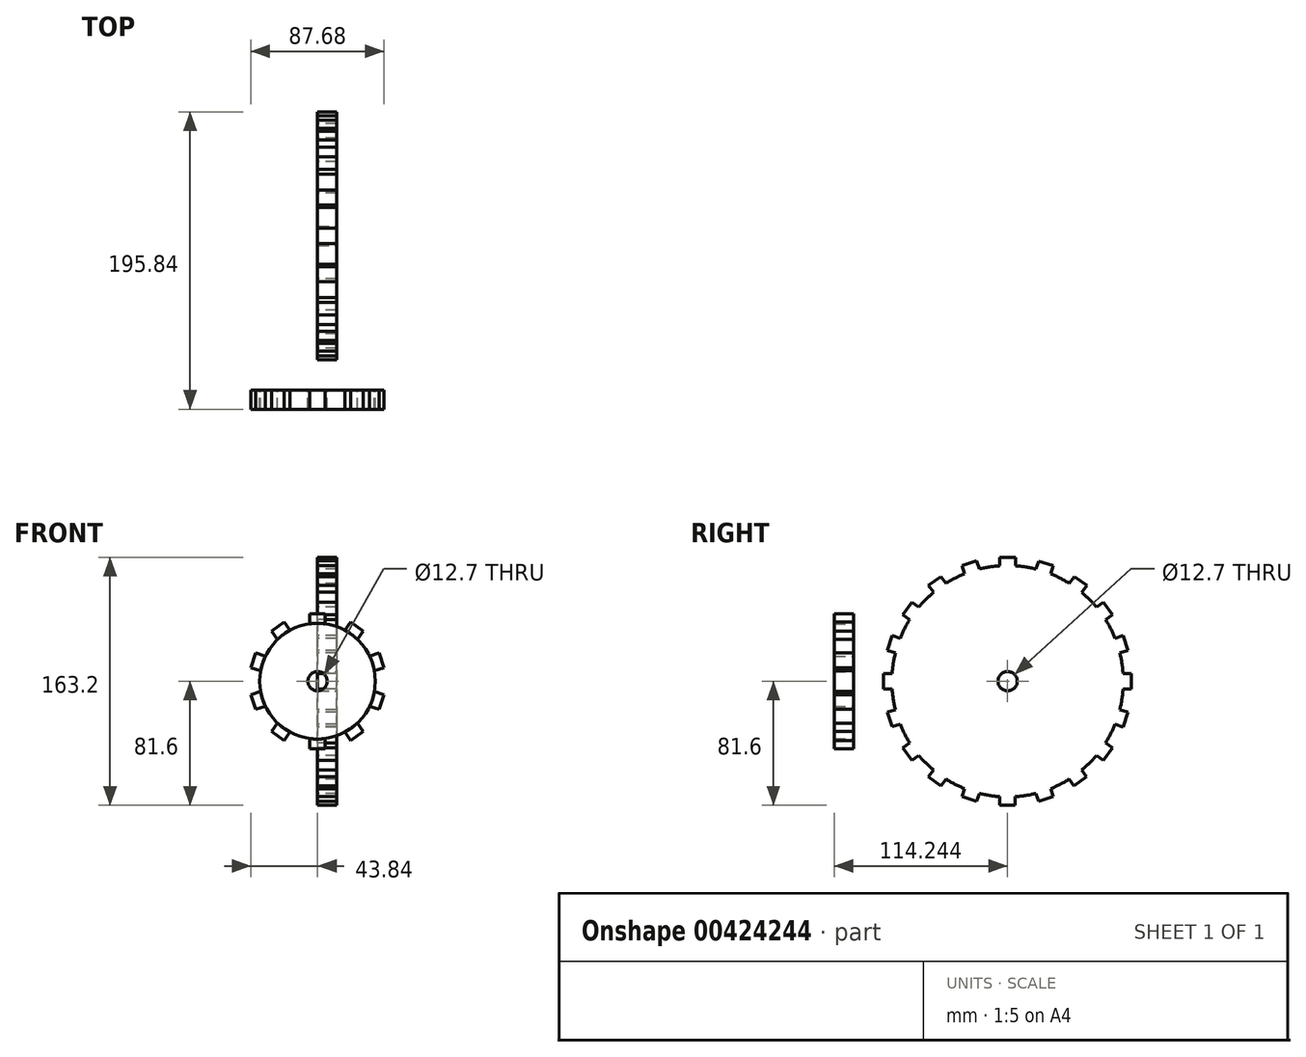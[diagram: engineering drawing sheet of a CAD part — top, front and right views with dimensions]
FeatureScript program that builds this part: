
annotation { "Feature Type Name" : "Feature", "Feature Type Description" : "" }
export const myFeature = defineFeature(function(context is Context, id is Id, definition is map)
    precondition{}
    {
        {
            var Q0;
            Q0=qCreatedBy(makeId("Front.planeOp"),FACE);
            var sketch = newSketch(context, id + "F0", { "sketchPlane" : qUnion([Q0])});
            skCircle(sketch, "E0", {"center": v(0, 0) * mm, "radius": 38.1 * mm});
            skSolve(sketch);
        }
        {
            var Q0;
            Q0=makeQuery(id+"F0.imprint","IMPRINT",FACE,{"disambiguationData":[TD([[makeQuery(id+"F0.imprint","IMPRINT",EDGE,{"derivedFrom":sQuery(id+"F0.wireOp",EDGE,"E0")}),1.0]])]});
            var sketch = newSketch(context, id + "F1", { "sketchPlane" : qUnion([Q0])});
            skLineSegment(sketch, "E1.bottom", {"start": v(-5.08, 36.83) * mm, "end": v(5.08, 36.83) * mm});
            skLineSegment(sketch, "E1.top", {"start": v(-5.08, 44.45) * mm, "end": v(5.08, 44.45) * mm});
            skLineSegment(sketch, "E1.left", {"start": v(-5.08, 36.83) * mm, "end": v(-5.08, 44.45) * mm});
            skLineSegment(sketch, "E1.right", {"start": v(5.08, 36.83) * mm, "end": v(5.08, 44.45) * mm});
            skSolve(sketch);
        }
        {
            var Q0;
            Q0 = qSketchRegion(id + "F0", true);
            var Q1;
            {var subQ0=sQuery(id+"F1.wireOp",EDGE,"E1.top");Q1=makeQuery(id+"F1.imprint","IMPRINT",FACE,{"disambiguationData":[TD([[makeQuery(id+"F1.imprint","IMPRINT",EDGE,{"derivedFrom":subQ0}),-1.0]])]});}
            extrude(context, id + "F2", {"entities" : qUnion([Q0, Q1]), "depth" : 12.7 * mm});
        }
        {
            var Q0;
            Q0=makeQuery(id+"F2.opExtrude","SWEPT_BODY",BODY,{"disambiguationData":[OSD([sQuery(id+"F0.wireOp",EDGE,"E0"),sQuery(id+"F1.wireOp",EDGE,"E1.top"),sQuery(id+"F1.wireOp",EDGE,"E1.left"),sQuery(id+"F1.wireOp",EDGE,"E1.right")])]});
            var Q1;
            Q1=sQuery(id+"F0.wireOp",EDGE,"E0");
            circularPattern(context, id + "F3", {"entities" : qUnion([Q0]), "axis" : qUnion([Q1]), "angle" : 360 * degree, "instanceCount" : 10, "equalSpace" : true});
        }
        {
            var Q0;
            Q0=sQuery(id+"F0.wireOp",VERTEX,"E0.center");
            var Q1;
            Q1=makeQuery(id+"F2.opExtrude","SWEPT_BODY",BODY,{"disambiguationData":[OSD([sQuery(id+"F0.wireOp",EDGE,"E0")])]});
            hole(context, id + "F4", {"style" : HoleStyle.SIMPLE, "endStyle" : HoleEndStyle.THROUGH, "oppositeDirection" : true, "holeDiameter" : 12.7 * mm, "tappedDepth" : 12.7 * mm, "tapClearance" : 3, "locations" : qUnion([Q0]), "scope" : qUnion([Q1])});
        }
        {
            var Q0;
            Q0=qCreatedBy(makeId("Right.planeOp"),FACE);
            var sketch = newSketch(context, id + "F5", { "sketchPlane" : qUnion([Q0])});
            skCircle(sketch, "E2", {"center": v(101.54, 0) * mm, "radius": 76.2 * mm});
            skSolve(sketch);
        }
        {
            var Q0;
            Q0=makeQuery(id+"F5.imprint","IMPRINT",FACE,{"disambiguationData":[TD([[makeQuery(id+"F5.imprint","IMPRINT",EDGE,{"derivedFrom":sQuery(id+"F5.wireOp",EDGE,"E2")}),1.0]])]});
            var sketch = newSketch(context, id + "F6", { "sketchPlane" : qUnion([Q0])});
            skLineSegment(sketch, "E3.bottom", {"start": v(96.49, 73.98) * mm, "end": v(106.65, 73.98) * mm});
            skLineSegment(sketch, "E3.top", {"start": v(96.49, 81.6) * mm, "end": v(106.65, 81.6) * mm});
            skLineSegment(sketch, "E3.left", {"start": v(96.49, 73.98) * mm, "end": v(96.49, 81.6) * mm});
            skLineSegment(sketch, "E3.right", {"start": v(106.65, 73.98) * mm, "end": v(106.65, 81.6) * mm});
            skSolve(sketch);
        }
        {
            var Q0;
            Q0=makeQuery(id+"F5.imprint","IMPRINT",FACE,{"disambiguationData":[TD([[makeQuery(id+"F5.imprint","IMPRINT",EDGE,{"derivedFrom":sQuery(id+"F5.wireOp",EDGE,"E2")}),1.0]])]});
            var Q1;
            Q1=makeQuery(id+"F6.imprint","IMPRINT",FACE,{"disambiguationData":[TD([[makeQuery(id+"F6.imprint","IMPRINT",EDGE,{"derivedFrom":sQuery(id+"F6.wireOp",EDGE,"E3.top")}),-1.0]])]});
            extrude(context, id + "F7", {"entities" : qUnion([Q0, Q1]), "depth" : 12.7 * mm});
        }
        {
            var Q0;
            Q0=makeQuery(id+"F7.opExtrude","SWEPT_BODY",BODY,{"disambiguationData":[OSD([sQuery(id+"F5.wireOp",EDGE,"E2"),sQuery(id+"F6.wireOp",EDGE,"E3.bottom"),sQuery(id+"F6.wireOp",EDGE,"E3.top"),sQuery(id+"F6.wireOp",EDGE,"E3.left"),sQuery(id+"F6.wireOp",EDGE,"E3.right")])]});
            var Q1;
            {var subQ0=sQuery(id+"F5.wireOp",EDGE,"E2");Q1=makeQuery(id+"F7.opExtrude","CAP_EDGE",EDGE,{"disambiguationData":[OSD([subQ0]),TDD([makeQuery(id+"F5.imprint","IMPRINT",EDGE,{"derivedFrom":subQ0})])],"isStart":false});}
            circularPattern(context, id + "F8", {"entities" : qUnion([Q0]), "axis" : qUnion([Q1]), "angle" : 360 * degree, "instanceCount" : 20, "equalSpace" : true});
        }
        {
            var Q0;
            Q0=makeQuery(id+"F8.opPattern","COPY",BODY,{"derivedFrom":makeQuery(id+"F7.opExtrude","SWEPT_BODY",BODY,{"disambiguationData":[OSD([sQuery(id+"F5.wireOp",EDGE,"E2"),sQuery(id+"F6.wireOp",EDGE,"E3.bottom"),sQuery(id+"F6.wireOp",EDGE,"E3.top"),sQuery(id+"F6.wireOp",EDGE,"E3.left"),sQuery(id+"F6.wireOp",EDGE,"E3.right")])]}),"instanceName":"1"});
            var Q1;
            Q1=makeQuery(id+"F8.opPattern","COPY",BODY,{"derivedFrom":makeQuery(id+"F7.opExtrude","SWEPT_BODY",BODY,{"disambiguationData":[OSD([sQuery(id+"F5.wireOp",EDGE,"E2"),sQuery(id+"F6.wireOp",EDGE,"E3.bottom"),sQuery(id+"F6.wireOp",EDGE,"E3.top"),sQuery(id+"F6.wireOp",EDGE,"E3.left"),sQuery(id+"F6.wireOp",EDGE,"E3.right")])]}),"instanceName":"2"});
            var Q2;
            Q2=makeQuery(id+"F7.opExtrude","SWEPT_BODY",BODY,{"disambiguationData":[OSD([sQuery(id+"F5.wireOp",EDGE,"E2")])]});
            var Q3;
            Q3=makeQuery(id+"F7.opExtrude","SWEPT_BODY",BODY,{"disambiguationData":[OSD([sQuery(id+"F5.wireOp",EDGE,"E2"),sQuery(id+"F6.wireOp",EDGE,"E3.bottom"),sQuery(id+"F6.wireOp",EDGE,"E3.top"),sQuery(id+"F6.wireOp",EDGE,"E3.left"),sQuery(id+"F6.wireOp",EDGE,"E3.right")])]});
            var Q4;
            Q4=makeQuery(id+"F8.opPattern","COPY",BODY,{"derivedFrom":makeQuery(id+"F7.opExtrude","SWEPT_BODY",BODY,{"disambiguationData":[OSD([sQuery(id+"F5.wireOp",EDGE,"E2"),sQuery(id+"F6.wireOp",EDGE,"E3.bottom"),sQuery(id+"F6.wireOp",EDGE,"E3.top"),sQuery(id+"F6.wireOp",EDGE,"E3.left"),sQuery(id+"F6.wireOp",EDGE,"E3.right")])]}),"instanceName":"9"});
            var Q5;
            Q5=makeQuery(id+"F8.opPattern","COPY",BODY,{"derivedFrom":makeQuery(id+"F7.opExtrude","SWEPT_BODY",BODY,{"disambiguationData":[OSD([sQuery(id+"F5.wireOp",EDGE,"E2"),sQuery(id+"F6.wireOp",EDGE,"E3.bottom"),sQuery(id+"F6.wireOp",EDGE,"E3.top"),sQuery(id+"F6.wireOp",EDGE,"E3.left"),sQuery(id+"F6.wireOp",EDGE,"E3.right")])]}),"instanceName":"8"});
            var Q6;
            Q6=makeQuery(id+"F8.opPattern","COPY",BODY,{"derivedFrom":makeQuery(id+"F7.opExtrude","SWEPT_BODY",BODY,{"disambiguationData":[OSD([sQuery(id+"F5.wireOp",EDGE,"E2"),sQuery(id+"F6.wireOp",EDGE,"E3.bottom"),sQuery(id+"F6.wireOp",EDGE,"E3.top"),sQuery(id+"F6.wireOp",EDGE,"E3.left"),sQuery(id+"F6.wireOp",EDGE,"E3.right")])]}),"instanceName":"7"});
            var Q7;
            Q7=makeQuery(id+"F8.opPattern","COPY",BODY,{"derivedFrom":makeQuery(id+"F7.opExtrude","SWEPT_BODY",BODY,{"disambiguationData":[OSD([sQuery(id+"F5.wireOp",EDGE,"E2"),sQuery(id+"F6.wireOp",EDGE,"E3.bottom"),sQuery(id+"F6.wireOp",EDGE,"E3.top"),sQuery(id+"F6.wireOp",EDGE,"E3.left"),sQuery(id+"F6.wireOp",EDGE,"E3.right")])]}),"instanceName":"6"});
            var Q8;
            Q8=makeQuery(id+"F8.opPattern","COPY",BODY,{"derivedFrom":makeQuery(id+"F7.opExtrude","SWEPT_BODY",BODY,{"disambiguationData":[OSD([sQuery(id+"F5.wireOp",EDGE,"E2"),sQuery(id+"F6.wireOp",EDGE,"E3.bottom"),sQuery(id+"F6.wireOp",EDGE,"E3.top"),sQuery(id+"F6.wireOp",EDGE,"E3.left"),sQuery(id+"F6.wireOp",EDGE,"E3.right")])]}),"instanceName":"5"});
            var Q9;
            Q9=makeQuery(id+"F8.opPattern","COPY",BODY,{"derivedFrom":makeQuery(id+"F7.opExtrude","SWEPT_BODY",BODY,{"disambiguationData":[OSD([sQuery(id+"F5.wireOp",EDGE,"E2"),sQuery(id+"F6.wireOp",EDGE,"E3.bottom"),sQuery(id+"F6.wireOp",EDGE,"E3.top"),sQuery(id+"F6.wireOp",EDGE,"E3.left"),sQuery(id+"F6.wireOp",EDGE,"E3.right")])]}),"instanceName":"4"});
            var Q10;
            Q10=makeQuery(id+"F8.opPattern","COPY",BODY,{"derivedFrom":makeQuery(id+"F7.opExtrude","SWEPT_BODY",BODY,{"disambiguationData":[OSD([sQuery(id+"F5.wireOp",EDGE,"E2"),sQuery(id+"F6.wireOp",EDGE,"E3.bottom"),sQuery(id+"F6.wireOp",EDGE,"E3.top"),sQuery(id+"F6.wireOp",EDGE,"E3.left"),sQuery(id+"F6.wireOp",EDGE,"E3.right")])]}),"instanceName":"3"});
            var Q11;
            Q11=makeQuery(id+"F8.opPattern","COPY",BODY,{"derivedFrom":makeQuery(id+"F7.opExtrude","SWEPT_BODY",BODY,{"disambiguationData":[OSD([sQuery(id+"F5.wireOp",EDGE,"E2"),sQuery(id+"F6.wireOp",EDGE,"E3.top"),sQuery(id+"F6.wireOp",EDGE,"E3.left"),sQuery(id+"F6.wireOp",EDGE,"E3.right")])]}),"instanceName":"19"});
            var Q12;
            Q12=makeQuery(id+"F8.opPattern","COPY",BODY,{"derivedFrom":makeQuery(id+"F7.opExtrude","SWEPT_BODY",BODY,{"disambiguationData":[OSD([sQuery(id+"F5.wireOp",EDGE,"E2"),sQuery(id+"F6.wireOp",EDGE,"E3.top"),sQuery(id+"F6.wireOp",EDGE,"E3.left"),sQuery(id+"F6.wireOp",EDGE,"E3.right")])]}),"instanceName":"18"});
            var Q13;
            Q13=makeQuery(id+"F8.opPattern","COPY",BODY,{"derivedFrom":makeQuery(id+"F7.opExtrude","SWEPT_BODY",BODY,{"disambiguationData":[OSD([sQuery(id+"F5.wireOp",EDGE,"E2"),sQuery(id+"F6.wireOp",EDGE,"E3.top"),sQuery(id+"F6.wireOp",EDGE,"E3.left"),sQuery(id+"F6.wireOp",EDGE,"E3.right")])]}),"instanceName":"17"});
            var Q14;
            Q14=makeQuery(id+"F8.opPattern","COPY",BODY,{"derivedFrom":makeQuery(id+"F7.opExtrude","SWEPT_BODY",BODY,{"disambiguationData":[OSD([sQuery(id+"F5.wireOp",EDGE,"E2"),sQuery(id+"F6.wireOp",EDGE,"E3.top"),sQuery(id+"F6.wireOp",EDGE,"E3.left"),sQuery(id+"F6.wireOp",EDGE,"E3.right")])]}),"instanceName":"16"});
            var Q15;
            Q15=makeQuery(id+"F8.opPattern","COPY",BODY,{"derivedFrom":makeQuery(id+"F7.opExtrude","SWEPT_BODY",BODY,{"disambiguationData":[OSD([sQuery(id+"F5.wireOp",EDGE,"E2"),sQuery(id+"F6.wireOp",EDGE,"E3.top"),sQuery(id+"F6.wireOp",EDGE,"E3.left"),sQuery(id+"F6.wireOp",EDGE,"E3.right")])]}),"instanceName":"15"});
            var Q16;
            Q16=makeQuery(id+"F8.opPattern","COPY",BODY,{"derivedFrom":makeQuery(id+"F7.opExtrude","SWEPT_BODY",BODY,{"disambiguationData":[OSD([sQuery(id+"F5.wireOp",EDGE,"E2"),sQuery(id+"F6.wireOp",EDGE,"E3.top"),sQuery(id+"F6.wireOp",EDGE,"E3.left"),sQuery(id+"F6.wireOp",EDGE,"E3.right")])]}),"instanceName":"14"});
            var Q17;
            Q17=makeQuery(id+"F8.opPattern","COPY",BODY,{"derivedFrom":makeQuery(id+"F7.opExtrude","SWEPT_BODY",BODY,{"disambiguationData":[OSD([sQuery(id+"F5.wireOp",EDGE,"E2"),sQuery(id+"F6.wireOp",EDGE,"E3.top"),sQuery(id+"F6.wireOp",EDGE,"E3.left"),sQuery(id+"F6.wireOp",EDGE,"E3.right")])]}),"instanceName":"13"});
            var Q18;
            Q18=makeQuery(id+"F8.opPattern","COPY",BODY,{"derivedFrom":makeQuery(id+"F7.opExtrude","SWEPT_BODY",BODY,{"disambiguationData":[OSD([sQuery(id+"F5.wireOp",EDGE,"E2"),sQuery(id+"F6.wireOp",EDGE,"E3.top"),sQuery(id+"F6.wireOp",EDGE,"E3.left"),sQuery(id+"F6.wireOp",EDGE,"E3.right")])]}),"instanceName":"12"});
            var Q19;
            Q19=makeQuery(id+"F8.opPattern","COPY",BODY,{"derivedFrom":makeQuery(id+"F7.opExtrude","SWEPT_BODY",BODY,{"disambiguationData":[OSD([sQuery(id+"F5.wireOp",EDGE,"E2"),sQuery(id+"F6.wireOp",EDGE,"E3.top"),sQuery(id+"F6.wireOp",EDGE,"E3.left"),sQuery(id+"F6.wireOp",EDGE,"E3.right")])]}),"instanceName":"11"});
            var Q20;
            Q20=makeQuery(id+"F8.opPattern","COPY",BODY,{"derivedFrom":makeQuery(id+"F7.opExtrude","SWEPT_BODY",BODY,{"disambiguationData":[OSD([sQuery(id+"F5.wireOp",EDGE,"E2"),sQuery(id+"F6.wireOp",EDGE,"E3.top"),sQuery(id+"F6.wireOp",EDGE,"E3.left"),sQuery(id+"F6.wireOp",EDGE,"E3.right")])]}),"instanceName":"10"});
            booleanBodies(context, id + "F9", {"operationType" : BooleanOperationType.UNION, "tools" : qUnion([Q0, Q1, Q2, Q3, Q4, Q5, Q6, Q7, Q8, Q9, Q10, Q11, Q12, Q13, Q14, Q15, Q16, Q17, Q18, Q19, Q20])});
        }
        {
            var Q0;
            {var subQ0=sQuery(id+"F5.wireOp",EDGE,"E2");var subQ1=makeQuery(id+"F7.opExtrude","CAP_FACE",FACE,{"disambiguationData":[OSD([subQ0,sQuery(id+"F6.wireOp",EDGE,"E3.top"),sQuery(id+"F6.wireOp",EDGE,"E3.left"),sQuery(id+"F6.wireOp",EDGE,"E3.right")])],"isStart":false});Q0=makeQuery(id+"F9.opBoolean","MERGE",FACE,{"derivedFrom":[makeQuery(id+"F7.opExtrude","CAP_FACE",FACE,{"disambiguationData":[OSD([subQ0])],"isStart":false}),subQ1,makeQuery(id+"F8.opPattern","COPY",FACE,{"derivedFrom":subQ1,"instanceName":"1"}),makeQuery(id+"F8.opPattern","COPY",FACE,{"derivedFrom":subQ1,"instanceName":"2"}),makeQuery(id+"F8.opPattern","COPY",FACE,{"derivedFrom":subQ1,"instanceName":"3"}),makeQuery(id+"F8.opPattern","COPY",FACE,{"derivedFrom":subQ1,"instanceName":"4"}),makeQuery(id+"F8.opPattern","COPY",FACE,{"derivedFrom":subQ1,"instanceName":"5"}),makeQuery(id+"F8.opPattern","COPY",FACE,{"derivedFrom":subQ1,"instanceName":"6"}),makeQuery(id+"F8.opPattern","COPY",FACE,{"derivedFrom":subQ1,"instanceName":"7"}),makeQuery(id+"F8.opPattern","COPY",FACE,{"derivedFrom":subQ1,"instanceName":"8"}),makeQuery(id+"F8.opPattern","COPY",FACE,{"derivedFrom":subQ1,"instanceName":"9"})]});}
            var sketch = newSketch(context, id + "F10", { "sketchPlane" : qUnion([Q0])});
            skPoint(sketch, "E4", {"position": v(101.54, 0) * mm});
            skSolve(sketch);
        }
        {
            var Q0;
            Q0=sQuery(id+"F10.wireOp",VERTEX,"E4");
            var Q1;
            Q1=makeQuery(id+"F8.opPattern","COPY",BODY,{"derivedFrom":makeQuery(id+"F7.opExtrude","SWEPT_BODY",BODY,{"disambiguationData":[OSD([sQuery(id+"F5.wireOp",EDGE,"E2"),sQuery(id+"F6.wireOp",EDGE,"E3.top"),sQuery(id+"F6.wireOp",EDGE,"E3.left"),sQuery(id+"F6.wireOp",EDGE,"E3.right")])]}),"instanceName":"1"});
            hole(context, id + "F11", {"style" : HoleStyle.SIMPLE, "endStyle" : HoleEndStyle.THROUGH, "holeDiameter" : 12.7 * mm, "tappedDepth" : 12.7 * mm, "tapClearance" : 3, "locations" : qUnion([Q0]), "scope" : qUnion([Q1])});
        }
    });
